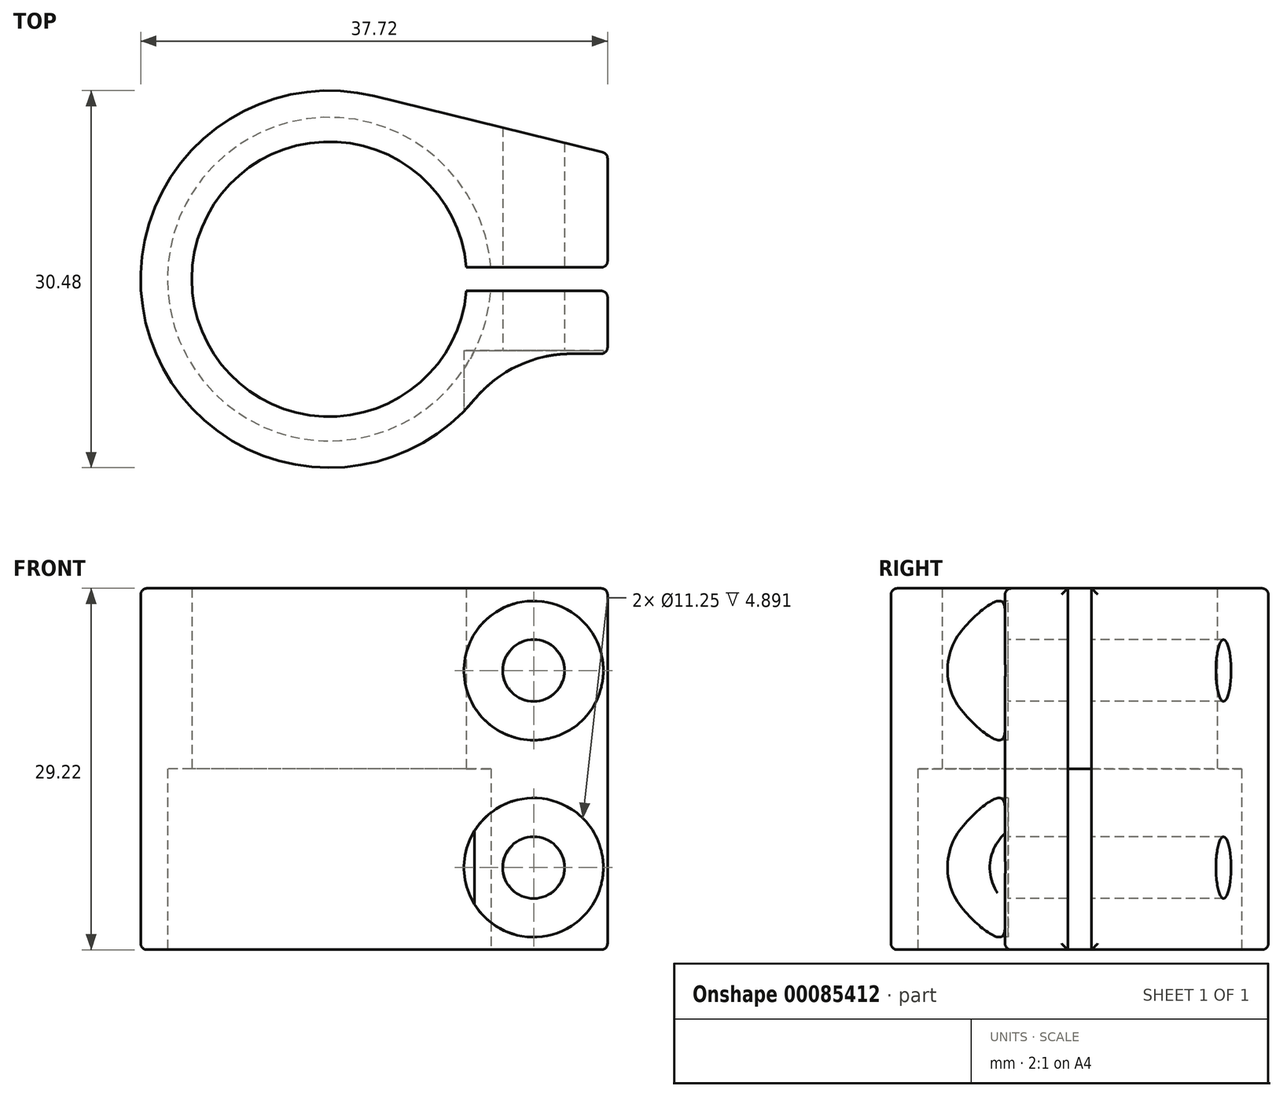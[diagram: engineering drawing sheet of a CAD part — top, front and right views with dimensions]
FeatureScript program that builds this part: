
annotation { "Feature Type Name" : "Feature", "Feature Type Description" : "" }
export const myFeature = defineFeature(function(context is Context, id is Id, definition is map)
    precondition{}
    {
        {
            var Q0;
            Q0=qCreatedBy(makeId("Top.planeOp"),FACE);
            var sketch = newSketch(context, id + "F0", { "sketchPlane" : qUnion([Q0])});
            skArc(sketch, "E0", {"start": v(13.05, 0.95) * mm, "mid": v(-13.08, 0) * mm, "end": v(13.05, -0.95) * mm});
            skArc(sketch, "E1", {"start": v(11.07, 0.95) * mm, "mid": v(-11.11, 0) * mm, "end": v(11.07, -0.95) * mm});
            skArc(sketch, "E2.0", {"start": v(3.64, 14.8) * mm, "mid": v(-14.47, -4.78) * mm, "end": v(11.74, -9.72) * mm});
            skLineSegment(sketch, "E3.bottom", {"start": v(-105.09, 35.44) * mm, "end": v(-90.3, 35.44) * mm});
            skLineSegment(sketch, "E3.top", {"start": v(-105.09, 27.03) * mm, "end": v(-90.3, 27.03) * mm});
            skLineSegment(sketch, "E3.left", {"start": v(-105.09, 35.44) * mm, "end": v(-105.09, 27.03) * mm});
            skLineSegment(sketch, "E3.right", {"start": v(-90.3, 35.44) * mm, "end": v(-90.3, 27.03) * mm});
            skLineSegment(sketch, "E4.bottom", {"start": v(11.07, 0.95) * mm, "end": v(22.48, 0.95) * mm});
            skLineSegment(sketch, "E4.top", {"start": v(11.07, -0.95) * mm, "end": v(22.48, -0.95) * mm});
            skLineSegment(sketch, "E5", {"start": v(22.48, 10.16) * mm, "end": v(22.48, 0.95) * mm});
            skLineSegment(sketch, "E6", {"start": v(22.48, 10.16) * mm, "end": v(3.64, 14.8) * mm});
            skLineSegment(sketch, "E7.trimOffspring", {"start": v(22.48, -0.95) * mm, "end": v(22.48, -6.03) * mm});
            skLineSegment(sketch, "E8", {"start": v(19.57, -6.03) * mm, "end": v(22.48, -6.03) * mm});
            skArc(sketch, "E9.filletArc", {"start": v(19.57, -6.03) * mm, "mid": v(15.24, -7) * mm, "end": v(11.74, -9.72) * mm});
            skSolve(sketch);
        }
        {
            var Q0;
            {var subQ0=sQuery(id+"F0.wireOp",EDGE,"E6");Q0=makeQuery(id+"F0.imprint","IMPRINT",FACE,{"disambiguationData":[TD([[makeQuery(id+"F0.imprint","IMPRINT",EDGE,{"derivedFrom":subQ0}),1.0]])]});}
            var Q1;
            {var subQ0=sQuery(id+"F0.wireOp",EDGE,"5RjW3dUI-Fn9Q-mEde-UQQJ-QF3pORbWQ2Yy");Q1=makeQuery(id+"F0.imprint","IMPRINT",FACE,{"disambiguationData":[TD([[makeQuery(id+"F0.imprint","IMPRINT",EDGE,{"derivedFrom":subQ0}),-1.0]])]});}
            var Q2;
            {var subQ0=sQuery(id+"F0.wireOp",EDGE,"E6");Q2=makeQuery(id+"F0.imprint","IMPRINT",FACE,{"disambiguationData":[TD([[makeQuery(id+"F0.imprint","IMPRINT",EDGE,{"derivedFrom":subQ0}),1.0]])]});}
            var Q3;
            {var subQ0=sQuery(id+"F0.wireOp",EDGE,"5RjW3dUI-Fn9Q-mEde-UQQJ-QF3pORbWQ2Yy");Q3=makeQuery(id+"F0.imprint","IMPRINT",FACE,{"disambiguationData":[TD([[makeQuery(id+"F0.imprint","IMPRINT",EDGE,{"derivedFrom":subQ0}),-1.0]])]});}
            var Q4;
            {var subQ0=sQuery(id+"F0.wireOp",EDGE,"E6");Q4=makeQuery(id+"F0.imprint","IMPRINT",FACE,{"disambiguationData":[TD([[makeQuery(id+"F0.imprint","IMPRINT",EDGE,{"derivedFrom":subQ0}),1.0]])]});}
            var Q5;
            {var subQ0=sQuery(id+"F0.wireOp",EDGE,"5RjW3dUI-Fn9Q-mEde-UQQJ-QF3pORbWQ2Yy");Q5=makeQuery(id+"F0.imprint","IMPRINT",FACE,{"disambiguationData":[TD([[makeQuery(id+"F0.imprint","IMPRINT",EDGE,{"derivedFrom":subQ0}),-1.0]])]});}
            var Q6;
            {var subQ0=sQuery(id+"F0.wireOp",EDGE,"E6");Q6=makeQuery(id+"F0.imprint","IMPRINT",FACE,{"disambiguationData":[TD([[makeQuery(id+"F0.imprint","IMPRINT",EDGE,{"derivedFrom":subQ0}),1.0]])]});}
            var Q7;
            {var subQ0=sQuery(id+"F0.wireOp",EDGE,"5RjW3dUI-Fn9Q-mEde-UQQJ-QF3pORbWQ2Yy");Q7=makeQuery(id+"F0.imprint","IMPRINT",FACE,{"disambiguationData":[TD([[makeQuery(id+"F0.imprint","IMPRINT",EDGE,{"derivedFrom":subQ0}),-1.0]])]});}
            var Q8;
            {var subQ5=sQuery(id+"F0.wireOp",EDGE,"E4.bottom");var subQ7=sQuery(id+"F0.wireOp",EDGE,"E0");var subQ8=makeQuery(id+"F0.imprint","INTERSECT",VERTEX,{"derivedFrom":[subQ7,subQ5]});Q8=makeQuery(id+"F0.imprint","IMPRINT",FACE,{"disambiguationData":[TD([[makeQuery(id+"F0.imprint","IMPRINT",EDGE,{"disambiguationData":[TD([[subQ8,-1.0]])],"derivedFrom":subQ7}),-1.0]])]});}
            var Q9;
            {var subQ0=sQuery(id+"F0.wireOp",EDGE,"E6");Q9=makeQuery(id+"F0.imprint","IMPRINT",FACE,{"disambiguationData":[TD([[makeQuery(id+"F0.imprint","IMPRINT",EDGE,{"derivedFrom":subQ0}),1.0]])]});}
            var Q10;
            {var subQ0=sQuery(id+"F0.wireOp",EDGE,"E6");Q10=makeQuery(id+"F0.imprint","IMPRINT",FACE,{"disambiguationData":[TD([[makeQuery(id+"F0.imprint","IMPRINT",EDGE,{"derivedFrom":subQ0}),1.0]])]});}
            var Q11;
            {var subQ0=sQuery(id+"F0.wireOp",EDGE,"5RjW3dUI-Fn9Q-mEde-UQQJ-QF3pORbWQ2Yy");Q11=makeQuery(id+"F0.imprint","IMPRINT",FACE,{"disambiguationData":[TD([[makeQuery(id+"F0.imprint","IMPRINT",EDGE,{"derivedFrom":subQ0}),-1.0]])]});}
            var Q12;
            {var subQ5=sQuery(id+"F0.wireOp",EDGE,"E4.bottom");var subQ7=sQuery(id+"F0.wireOp",EDGE,"E0");var subQ8=makeQuery(id+"F0.imprint","INTERSECT",VERTEX,{"derivedFrom":[subQ7,subQ5]});Q12=makeQuery(id+"F0.imprint","IMPRINT",FACE,{"disambiguationData":[TD([[makeQuery(id+"F0.imprint","IMPRINT",EDGE,{"disambiguationData":[TD([[subQ8,-1.0]])],"derivedFrom":subQ7}),-1.0]])]});}
            var Q13;
            {var subQ0=sQuery(id+"F0.wireOp",EDGE,"E6");Q13=makeQuery(id+"F0.imprint","IMPRINT",FACE,{"disambiguationData":[TD([[makeQuery(id+"F0.imprint","IMPRINT",EDGE,{"derivedFrom":subQ0}),1.0]])]});}
            var Q14;
            {var subQ0=sQuery(id+"F0.wireOp",EDGE,"5RjW3dUI-Fn9Q-mEde-UQQJ-QF3pORbWQ2Yy");Q14=makeQuery(id+"F0.imprint","IMPRINT",FACE,{"disambiguationData":[TD([[makeQuery(id+"F0.imprint","IMPRINT",EDGE,{"derivedFrom":subQ0}),-1.0]])]});}
            var Q15;
            {var subQ0=sQuery(id+"F0.wireOp",EDGE,"E4.bottom");var subQ1=sQuery(id+"F0.wireOp",EDGE,"E2.0");var subQ2=makeQuery(id+"F0.imprint","INTERSECT",VERTEX,{"derivedFrom":[subQ1,subQ0]});Q15=makeQuery(id+"F0.imprint","IMPRINT",FACE,{"disambiguationData":[TD([[makeQuery(id+"F0.imprint","IMPRINT",EDGE,{"disambiguationData":[TD([[subQ2,1.0]])],"derivedFrom":subQ1}),-1.0]])]});}
            var Q16;
            {var subQ5=sQuery(id+"F0.wireOp",EDGE,"E4.bottom");var subQ7=sQuery(id+"F0.wireOp",EDGE,"E0");var subQ8=makeQuery(id+"F0.imprint","INTERSECT",VERTEX,{"derivedFrom":[subQ7,subQ5]});Q16=makeQuery(id+"F0.imprint","IMPRINT",FACE,{"disambiguationData":[TD([[makeQuery(id+"F0.imprint","IMPRINT",EDGE,{"disambiguationData":[TD([[subQ8,-1.0]])],"derivedFrom":subQ7}),-1.0]])]});}
            var Q17;
            {var subQ0=sQuery(id+"F0.wireOp",EDGE,"E6");Q17=makeQuery(id+"F0.imprint","IMPRINT",FACE,{"disambiguationData":[TD([[makeQuery(id+"F0.imprint","IMPRINT",EDGE,{"derivedFrom":subQ0}),1.0]])]});}
            var Q18;
            {var subQ0=sQuery(id+"F0.wireOp",EDGE,"5RjW3dUI-Fn9Q-mEde-UQQJ-QF3pORbWQ2Yy");Q18=makeQuery(id+"F0.imprint","IMPRINT",FACE,{"disambiguationData":[TD([[makeQuery(id+"F0.imprint","IMPRINT",EDGE,{"derivedFrom":subQ0}),-1.0]])]});}
            var Q19;
            {var subQ0=sQuery(id+"F0.wireOp",EDGE,"5RjW3dUI-Fn9Q-mEde-UQQJ-QF3pORbWQ2Yy");Q19=makeQuery(id+"F0.imprint","IMPRINT",FACE,{"disambiguationData":[TD([[makeQuery(id+"F0.imprint","IMPRINT",EDGE,{"derivedFrom":subQ0}),-1.0]])]});}
            var Q20;
            {var subQ5=sQuery(id+"F0.wireOp",EDGE,"E4.bottom");var subQ7=sQuery(id+"F0.wireOp",EDGE,"E0");var subQ8=makeQuery(id+"F0.imprint","INTERSECT",VERTEX,{"derivedFrom":[subQ7,subQ5]});Q20=makeQuery(id+"F0.imprint","IMPRINT",FACE,{"disambiguationData":[TD([[makeQuery(id+"F0.imprint","IMPRINT",EDGE,{"disambiguationData":[TD([[subQ8,-1.0]])],"derivedFrom":subQ7}),-1.0]])]});}
            extrude(context, id + "F1", {"entities" : qUnion([Q0, Q1, Q2, Q3, Q4, Q5, Q6, Q7, Q8, Q9, Q10, Q11, Q12, Q13, Q14, Q15, Q16, Q17, Q18, Q19, Q20]), "endBound" : BoundingType.SYMMETRIC, "depth" : 29.2 * mm});
        }
        {
            var Q0;
            {var subQ0=sQuery(id+"F0.wireOp",EDGE,"E4.bottom");var subQ1=sQuery(id+"F0.wireOp",EDGE,"E0");var subQ2=makeQuery(id+"F0.imprint","INTERSECT",VERTEX,{"derivedFrom":[subQ1,subQ0]});Q0=makeQuery(id+"F0.imprint","IMPRINT",FACE,{"disambiguationData":[TD([[makeQuery(id+"F0.imprint","IMPRINT",EDGE,{"disambiguationData":[TD([[subQ2,-1.0]])],"derivedFrom":subQ1}),1.0]])]});}
            var Q1;
            Q1=makeQuery(id+"F1.opExtrude","CAP_FACE",FACE,{"disambiguationData":[OSD([sQuery(id+"F0.wireOp",EDGE,"E0"),sQuery(id+"F0.wireOp",EDGE,"E2.0"),sQuery(id+"F0.wireOp",EDGE,"E4.bottom"),sQuery(id+"F0.wireOp",EDGE,"E4.top"),sQuery(id+"F0.wireOp",EDGE,"E5"),sQuery(id+"F0.wireOp",EDGE,"E6"),sQuery(id+"F0.wireOp",EDGE,"5RjW3dUI-Fn9Q-mEde-UQQJ-QF3pORbWQ2Yy")])],"isStart":false});
            var Q2;
            Q2=makeQuery(id+"F1.opExtrude","SWEPT_BODY",BODY,{"disambiguationData":[OSD([sQuery(id+"F0.wireOp",EDGE,"E0"),sQuery(id+"F0.wireOp",EDGE,"E2.0"),sQuery(id+"F0.wireOp",EDGE,"E4.bottom"),sQuery(id+"F0.wireOp",EDGE,"E4.top"),sQuery(id+"F0.wireOp",EDGE,"E5"),sQuery(id+"F0.wireOp",EDGE,"E6"),sQuery(id+"F0.wireOp",EDGE,"5RjW3dUI-Fn9Q-mEde-UQQJ-QF3pORbWQ2Yy")])]});
            extrude(context, id + "F2", {"entities" : qUnion([Q0]), "operationType" : NewBodyOperationType.ADD, "endBound" : BoundingType.UP_TO_SURFACE, "endBoundEntityFace" : qUnion([Q1]), "endBoundEntityBody" : qUnion([Q2]), "depth" : 15.88 * mm});
        }
        {
            var Q0;
            Q0=qCreatedBy(makeId("Front.planeOp"),FACE);
            cPlane(context, id + "F3", {"entities" : qUnion([Q0]), "cplaneType" : CPlaneType.OFFSET, "offset" : 13.97 * mm, "width" : 152.4 * mm, "height" : 152.4 * mm});
        }
        {
            var Q0;
            Q0=qCreatedBy(id+"F3.planeOp",FACE);
            var sketch = newSketch(context, id + "F4", { "sketchPlane" : qUnion([Q0])});
            skPoint(sketch, "E10", {"position": v(16.51, 7.96) * mm});
            skLineSegment(sketch, "E11", {"start": v(16.51, 7.96) * mm, "end": v(16.51, -7.96) * mm});
            skPoint(sketch, "E12", {"position": v(16.51, 0) * mm});
            skLineSegment(sketch, "E13", {"start": v(0, 0) * mm, "end": v(24.59, 0) * mm, "construction": true});
            skSolve(sketch);
        }
        {
            var Q0;
            Q0=sQuery(id+"F4.wireOp",VERTEX,"E10");
            var Q1;
            Q1=sQuery(id+"F4.wireOp",VERTEX,"E11.end");
            var Q2;
            Q2=makeQuery(id+"F1.opExtrude","SWEPT_BODY",BODY,{"disambiguationData":[OSD([sQuery(id+"F0.wireOp",EDGE,"E0"),sQuery(id+"F0.wireOp",EDGE,"E2.0"),sQuery(id+"F0.wireOp",EDGE,"E4.bottom"),sQuery(id+"F0.wireOp",EDGE,"E4.top"),sQuery(id+"F0.wireOp",EDGE,"E5"),sQuery(id+"F0.wireOp",EDGE,"E6"),sQuery(id+"F0.wireOp",EDGE,"5RjW3dUI-Fn9Q-mEde-UQQJ-QF3pORbWQ2Yy")])]});
            hole(context, id + "F5", {"style" : HoleStyle.C_BORE, "endStyle" : HoleEndStyle.BLIND, "holeDiameter" : 5 * mm, "cBoreDiameter" : 11.25 * mm, "cBoreDepth" : 0.25 * mm, "holeDepth" : 25.4 * mm, "locations" : qUnion([Q0, Q1]), "scope" : qUnion([Q2])});
        }
        {
            var Q0;
            Q0=makeQuery(id+"F1.opExtrude","CAP_EDGE",EDGE,{"disambiguationData":[OSD([sQuery(id+"F0.wireOp",EDGE,"E2.0")])],"isStart":true});
            var Q1;
            {var subQ0=sQuery(id+"F0.wireOp",EDGE,"E5");Q1=makeQuery(id+"F1.opExtrude","CAP_EDGE",EDGE,{"disambiguationData":[OSD([subQ0]),TDD([makeQuery(id+"F0.imprint","IMPRINT",EDGE,{"disambiguationData":[TD([[makeQuery(id+"F0.imprint","INTERSECT",VERTEX,{"derivedFrom":[subQ0,sQuery(id+"F0.wireOp",EDGE,"E6")]}),-1.0]])],"derivedFrom":subQ0})])],"isStart":true});}
            var Q2;
            {var subQ0=sQuery(id+"F0.wireOp",EDGE,"E5");Q2=makeQuery(id+"F1.opExtrude","CAP_EDGE",EDGE,{"disambiguationData":[OSD([subQ0]),TDD([makeQuery(id+"F0.imprint","IMPRINT",EDGE,{"disambiguationData":[TD([[makeQuery(id+"F0.imprint","INTERSECT",VERTEX,{"derivedFrom":[subQ0,sQuery(id+"F0.wireOp",EDGE,"5RjW3dUI-Fn9Q-mEde-UQQJ-QF3pORbWQ2Yy")]}),1.0]])],"derivedFrom":subQ0})])],"isStart":true});}
            var Q3;
            {var subQ0=sQuery(id+"F0.wireOp",EDGE,"5RjW3dUI-Fn9Q-mEde-UQQJ-QF3pORbWQ2Yy");var subQ1=sQuery(id+"F0.wireOp",EDGE,"E5");var subQ2=sQuery(id+"F0.wireOp",EDGE,"E4.top");var subQ5=makeQuery(id+"F5.hole-0.opRevolve","SWEPT_FACE",FACE,{"disambiguationData":[OSD([sQuery(id+"F5.hole-0.sketch.wireOp",EDGE,"cbore_start_line_2")])]});Q3=makeQuery(id+"F5.hole-1.boolean.opBoolean","SPLIT",EDGE,{"disambiguationData":[TD([makeQuery(id+"F5.hole-0.boolean.opBoolean","COPY",FACE,{"derivedFrom":subQ5})])],"derivedFrom":makeQuery(id+"F5.hole-0.boolean.opBoolean","SPLIT",EDGE,{"disambiguationData":[TD([makeQuery(id+"F1.opExtrude","CAP_FACE",FACE,{"disambiguationData":[OSD([sQuery(id+"F0.wireOp",EDGE,"E0"),sQuery(id+"F0.wireOp",EDGE,"E2.0"),sQuery(id+"F0.wireOp",EDGE,"E4.bottom"),subQ2,subQ1,sQuery(id+"F0.wireOp",EDGE,"E6"),subQ0])],"isStart":true})])],"derivedFrom":makeQuery(id+"F1.opExtrude","SWEPT_EDGE",EDGE,{"disambiguationData":[OSD([subQ1,subQ0])]})})});}
            var Q4;
            {var subQ0=sQuery(id+"F0.wireOp",EDGE,"5RjW3dUI-Fn9Q-mEde-UQQJ-QF3pORbWQ2Yy");var subQ1=sQuery(id+"F0.wireOp",EDGE,"E5");var subQ2=sQuery(id+"F0.wireOp",EDGE,"E4.top");var subQ3=makeQuery(id+"F1.opExtrude","CAP_FACE",FACE,{"disambiguationData":[OSD([sQuery(id+"F0.wireOp",EDGE,"E0"),sQuery(id+"F0.wireOp",EDGE,"E2.0"),sQuery(id+"F0.wireOp",EDGE,"E4.bottom"),subQ2,subQ1,sQuery(id+"F0.wireOp",EDGE,"E6"),subQ0])],"isStart":true});Q4=makeQuery(id+"F5.hole-1.boolean.opBoolean","SPLIT",EDGE,{"disambiguationData":[TD([subQ3])],"derivedFrom":makeQuery(id+"F5.hole-0.boolean.opBoolean","SPLIT",EDGE,{"disambiguationData":[TD([subQ3])],"derivedFrom":makeQuery(id+"F1.opExtrude","SWEPT_EDGE",EDGE,{"disambiguationData":[OSD([subQ1,subQ0])]})})});}
            var Q5;
            {var subQ0=sQuery(id+"F0.wireOp",EDGE,"E4.top");var subQ1=sQuery(id+"F0.wireOp",EDGE,"E4.bottom");var subQ2=sQuery(id+"F0.wireOp",EDGE,"E0");var subQ3=sQuery(id+"F0.wireOp",EDGE,"5RjW3dUI-Fn9Q-mEde-UQQJ-QF3pORbWQ2Yy");var subQ4=sQuery(id+"F0.wireOp",EDGE,"E5");Q5=makeQuery(id+"F5.hole-0.boolean.opBoolean","SPLIT",EDGE,{"disambiguationData":[TD([makeQuery(id+"F2.opExtrude","CAP_FACE",FACE,{"disambiguationData":[OSD([subQ2,sQuery(id+"F0.wireOp",EDGE,"E1"),subQ1,subQ0])],"isStart":false})])],"derivedFrom":makeQuery(id+"F1.opExtrude","SWEPT_EDGE",EDGE,{"disambiguationData":[OSD([subQ4,subQ3])]})});}
            var Q6;
            {var subQ0=sQuery(id+"F0.wireOp",EDGE,"E5");Q6=makeQuery(id+"F1.opExtrude","CAP_EDGE",EDGE,{"disambiguationData":[OSD([subQ0]),TDD([makeQuery(id+"F0.imprint","IMPRINT",EDGE,{"disambiguationData":[TD([[makeQuery(id+"F0.imprint","INTERSECT",VERTEX,{"derivedFrom":[subQ0,sQuery(id+"F0.wireOp",EDGE,"5RjW3dUI-Fn9Q-mEde-UQQJ-QF3pORbWQ2Yy")]}),1.0]])],"derivedFrom":subQ0})])],"isStart":false});}
            var Q7;
            {var subQ0=sQuery(id+"F0.wireOp",EDGE,"E5");Q7=makeQuery(id+"F1.opExtrude","CAP_EDGE",EDGE,{"disambiguationData":[OSD([subQ0]),TDD([makeQuery(id+"F0.imprint","IMPRINT",EDGE,{"disambiguationData":[TD([[makeQuery(id+"F0.imprint","INTERSECT",VERTEX,{"derivedFrom":[subQ0,sQuery(id+"F0.wireOp",EDGE,"E6")]}),-1.0]])],"derivedFrom":subQ0})])],"isStart":false});}
            var Q8;
            Q8=makeQuery(id+"F1.opExtrude","SWEPT_EDGE",EDGE,{"disambiguationData":[OSD([sQuery(id+"F0.wireOp",EDGE,"E5"),sQuery(id+"F0.wireOp",EDGE,"E6")])]});
            var Q9;
            Q9=makeQuery(id+"F1.opExtrude","CAP_EDGE",EDGE,{"disambiguationData":[OSD([sQuery(id+"F0.wireOp",EDGE,"E2.0")])],"isStart":false});
            var Q10;
            Q10=makeQuery(id+"F1.opExtrude","CAP_EDGE",EDGE,{"disambiguationData":[OSD([sQuery(id+"F0.wireOp",EDGE,"5RjW3dUI-Fn9Q-mEde-UQQJ-QF3pORbWQ2Yy")])],"isStart":false});
            var Q11;
            Q11=makeQuery(id+"F1.opExtrude","CAP_EDGE",EDGE,{"disambiguationData":[OSD([sQuery(id+"F0.wireOp",EDGE,"E6")])],"isStart":false});
            fillet(context, id + "F6", {"entities" : qUnion([Q0, Q1, Q2, Q3, Q4, Q5, Q6, Q7, Q8, Q9, Q10, Q11]), "radius" : 0.5 * mm, "tangentPropagation" : true, "allowEdgeOverflow" : false});
        }
        {
            var Q0;
            Q0=makeQuery(id+"F1.opExtrude","SWEPT_EDGE",EDGE,{"disambiguationData":[OSD([sQuery(id+"F0.wireOp",EDGE,"E7.trimOffspring"),sQuery(id+"F0.wireOp",EDGE,"E8")])]});
            var Q1;
            Q1=makeQuery(id+"F1.opExtrude","SWEPT_EDGE",EDGE,{"disambiguationData":[OSD([sQuery(id+"F0.wireOp",EDGE,"E4.top"),sQuery(id+"F0.wireOp",EDGE,"E7.trimOffspring")])]});
            fillet(context, id + "F7", {"entities" : qUnion([Q0, Q1]), "radius" : 0.5 * mm, "tangentPropagation" : true, "allowEdgeOverflow" : false});
        }
    });
